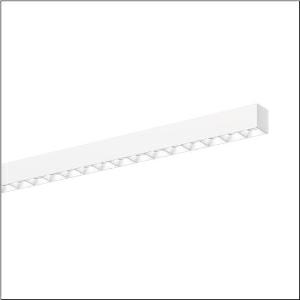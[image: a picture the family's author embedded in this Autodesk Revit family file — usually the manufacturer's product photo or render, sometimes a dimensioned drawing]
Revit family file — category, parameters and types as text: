
# Revit family: silica_r__21_51mx26dc3awb_8cf9
name_source: partatom
category: Lighting Fixtures
units: mm (PartAtom-declared; Revit-internal decimal feet)

## family parameters
Cut with Voids When Loaded = No
Host = Face
Light Source = No
Part Type = Normal
Room Calculation Point = No
Round Connector Dimension = Use Diameter
Shared = No

## types (1)
- --- (1 x LED, 10800 lm, 63.6 W, 3000K)
    Apparent Load = 64 VA
    CIE Flux Codes = 83 98 100 100 100
    Color Rendering = 80
    Color Temperature = 3000K
    Default Elevation = 1800 mm
    Description = Silica® 21, office luminaire, primary light control with darklight reflector, of PMMA, white, CAT 2 (L<= 3000cd/m²), light emission: direct distribution, primary light characteristic: symmetric, installation type: surface-mounted, LED, rated luminous flux: 10.800lm, luminous efficacy: 170lm/W, light colour: 830, colour temperature: 3000K, with terminal, 3+2-pole, max. 2.5mm², mains connection: 220..240V, AC, 50/60Hz, rated input power: 63.6W, luminaire housing, of aluminium, traffic white (RAL 9016), length: 3.004mm, width: 53mm, height: 53mm, protection rating (complete): IP20, insulation class (complete): insulation class I (protective earthing), certification: CE, permissible operating ambient temperature: 0..+35°C, standard: EN 50419, packaging unit: 1 piece
    Height = 0 mm  [stored 0 ft]
    Lamp = 1 x LED
    Lamp Light Flux = 10800 lm
    Lamp Power = 63.6 W
    Lamp count = 1
    Length = 3004 mm
    Luminous efficacy = 170 lm/W
    Manufacturer = Siteco
    ModVariant = No
    Model = 51MX26DC3AWB
    Mounting Place = Ceiling
    Mounting Type = Recessed
    Number of Poles = 1
    OnlyDefault = Yes
    Power Factor = 1
    Product Name = Silica® 21
    Product group = office luminaire | ceiling recessed
    ProductGroupID = 401
    Protection Class = Protection class I
    Protection Degree = IP 20
    RLX_Detail_Level = 1
    RLX_Emergency_Light_Flux = 0 lm
    RLX_Emergency_Type = 0
    RLX_Emergency_Type_DB = No
    RlxData = <blob elided: 58889 chars, md5=dac612dd>
    Socket = socket
    Standby Power = 0 W
    System Light Flux = 10800 lm
    System Power = 64 W
    Type Comments = factory setting: luminous flux: 100 % | dim-lin: 254 | 360 mA
    Type Image = l_1313597.jpg
    URL = http://relux.com
    VarID = @adj_073441
    Voltage = 0 V
    Weight = 0.00 kg
    Width = 53 mm

note: [stored X ft] marks values corroborated as IEEE doubles in the binary element streams (Revit-internal decimal feet)

## geometry (parser evidence)
native form markers: Blend x4, Sweep x13
no freeform markers — native parametric forms only
